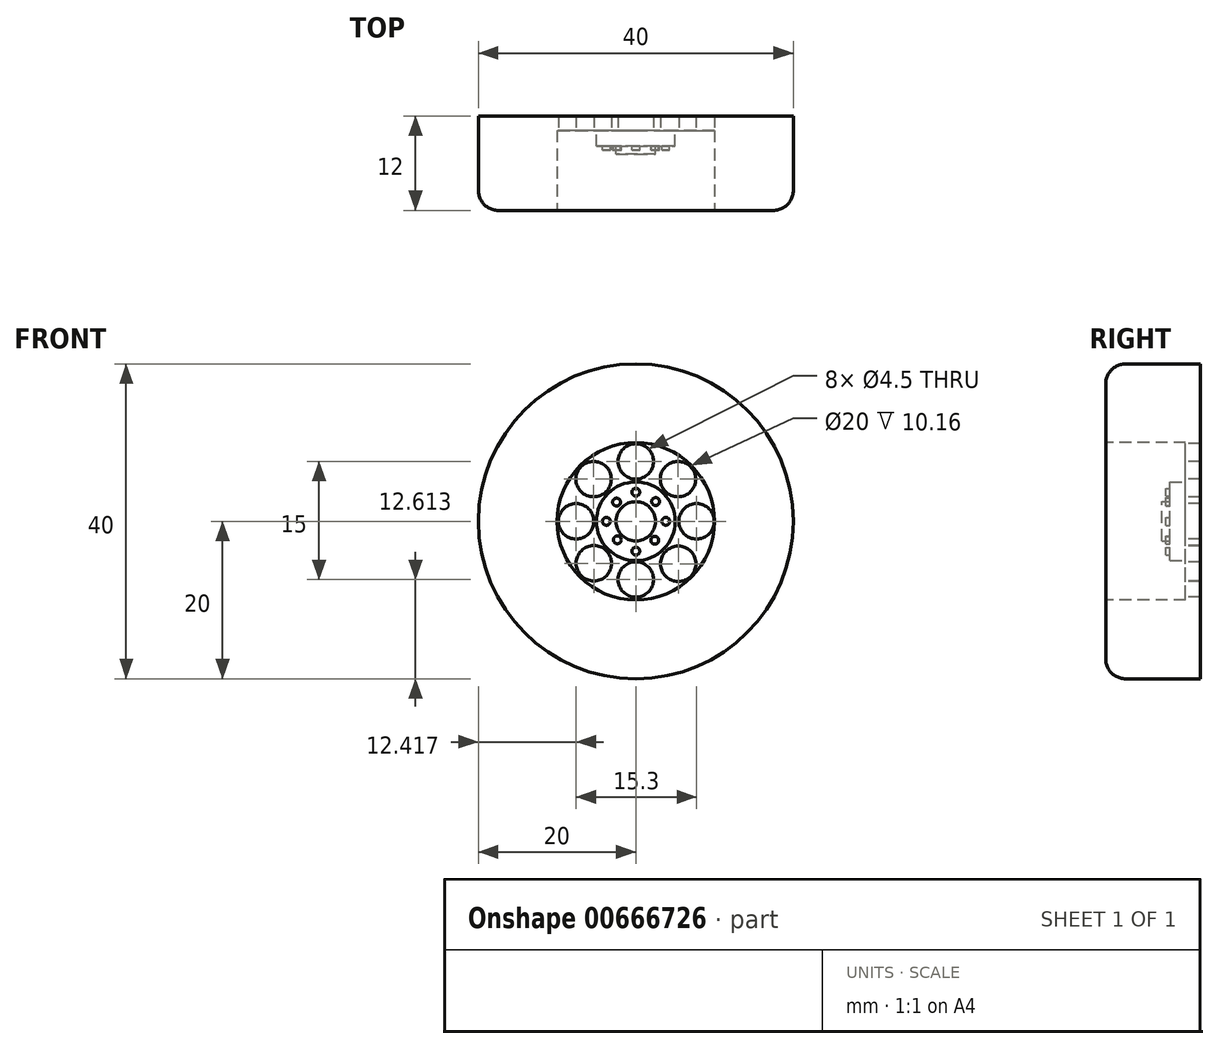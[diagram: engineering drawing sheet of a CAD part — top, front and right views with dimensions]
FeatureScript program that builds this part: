
annotation { "Feature Type Name" : "Feature", "Feature Type Description" : "" }
export const myFeature = defineFeature(function(context is Context, id is Id, definition is map)
    precondition{}
    {
        {
            var Q0;
            Q0=qCreatedBy(makeId("Front.planeOp"),FACE);
            var sketch = newSketch(context, id + "F0", { "sketchPlane" : qUnion([Q0])});
            skCircle(sketch, "E0", {"center": v(0, 0) * mm, "radius": 20 * mm});
            skSolve(sketch);
        }
        {
            var Q0;
            Q0=makeQuery(id+"F0.imprint","IMPRINT",FACE,{"disambiguationData":[TD([[makeQuery(id+"F0.imprint","IMPRINT",EDGE,{"derivedFrom":sQuery(id+"F0.wireOp",EDGE,"E0")}),1.0]])]});
            extrude(context, id + "F1", {"entities" : qUnion([Q0]), "depth" : 12 * mm, "offsetDistance" : 25.4 * mm});
        }
        {
            var Q0;
            Q0=makeQuery(id+"F1.opExtrude","CAP_FACE",FACE,{"disambiguationData":[OSD([sQuery(id+"F0.wireOp",EDGE,"E0")])],"isStart":false});
            fillet(context, id + "F2", {"entities" : qUnion([Q0]), "radius" : 2.54 * mm, "tangentPropagation" : true, "allowEdgeOverflow" : false});
        }
        {
            var Q0;
            Q0=makeQuery(id+"F1.opExtrude","CAP_FACE",FACE,{"disambiguationData":[OSD([sQuery(id+"F0.wireOp",EDGE,"E0")])],"isStart":false});
            var sketch = newSketch(context, id + "F3", { "sketchPlane" : qUnion([Q0])});
            skCircle(sketch, "E1", {"center": v(0, 0) * mm, "radius": 10 * mm});
            skSolve(sketch);
        }
        {
            var Q0;
            Q0=makeQuery(id+"F3.imprint","IMPRINT",FACE,{"disambiguationData":[TD([[makeQuery(id+"F3.imprint","IMPRINT",EDGE,{"derivedFrom":sQuery(id+"F3.wireOp",EDGE,"E1")}),1.0]])]});
            extrude(context, id + "F4", {"entities" : qUnion([Q0]), "operationType" : NewBodyOperationType.REMOVE, "oppositeDirection" : true, "depth" : 10.16 * mm, "offsetDistance" : 25.4 * mm});
        }
        {
            var Q0;
            Q0=makeQuery(id+"F4.boolean.opBoolean","COPY",FACE,{"derivedFrom":makeQuery(id+"F4.opExtrude","CAP_FACE",FACE,{"disambiguationData":[OSD([sQuery(id+"F3.wireOp",EDGE,"E1")])],"isStart":false})});
            var sketch = newSketch(context, id + "F5", { "sketchPlane" : qUnion([Q0])});
            skCircle(sketch, "E2.0.0", {"center": v(0, 0) * mm, "radius": 10 * mm});
            skCircle(sketch, "E3", {"center": v(0, 0) * mm, "radius": 5 * mm});
            skSolve(sketch);
        }
        {
            var Q0;
            Q0=makeQuery(id+"F5.imprint","IMPRINT",FACE,{"disambiguationData":[TD([[makeQuery(id+"F5.imprint","IMPRINT",EDGE,{"derivedFrom":sQuery(id+"F5.wireOp",EDGE,"E3")}),1.0]])]});
            extrude(context, id + "F6", {"entities" : qUnion([Q0]), "operationType" : NewBodyOperationType.ADD, "depth" : 2 * mm, "offsetDistance" : 25.4 * mm});
        }
        {
            var Q0;
            Q0=makeQuery(id+"F6.opExtrude","CAP_FACE",FACE,{"disambiguationData":[OSD([sQuery(id+"F5.wireOp",EDGE,"E3")])],"isStart":false});
            var sketch = newSketch(context, id + "F7", { "sketchPlane" : qUnion([Q0])});
            skCircle(sketch, "E4.0.0", {"center": v(0, 0) * mm, "radius": 5 * mm});
            skCircle(sketch, "E5", {"center": v(0, 0) * mm, "radius": 2.5 * mm});
            skSolve(sketch);
        }
        {
            var Q0;
            Q0=makeQuery(id+"F7.imprint","IMPRINT",FACE,{"disambiguationData":[TD([[makeQuery(id+"F7.imprint","IMPRINT",EDGE,{"derivedFrom":sQuery(id+"F7.wireOp",EDGE,"E5")}),1.0]])]});
            extrude(context, id + "F8", {"entities" : qUnion([Q0]), "operationType" : NewBodyOperationType.ADD, "depth" : 1 * mm, "offsetDistance" : 25.4 * mm});
        }
        {
            var Q0;
            Q0=makeQuery(id+"F4.boolean.opBoolean","COPY",FACE,{"derivedFrom":makeQuery(id+"F4.opExtrude","CAP_FACE",FACE,{"disambiguationData":[OSD([sQuery(id+"F3.wireOp",EDGE,"E1")])],"isStart":false})});
            var sketch = newSketch(context, id + "F9", { "sketchPlane" : qUnion([Q0])});
            skLineSegment(sketch, "E6", {"start": v(-7.58, 0) * mm, "end": v(7.72, 0) * mm});
            skLineSegment(sketch, "E7", {"start": v(0, 7.61) * mm, "end": v(0, -7.39) * mm});
            skSolve(sketch);
        }
        {
            var Q0;
            Q0=makeQuery(id+"F9.imprint","IMPRINT",FACE,{"disambiguationData":[TD([[makeQuery(id+"F9.imprint","IMPRINT",EDGE,{"derivedFrom":makeQuery(id+"F4.boolean.opBoolean","COPY",EDGE,{"derivedFrom":makeQuery(id+"F4.opExtrude","CAP_EDGE",EDGE,{"disambiguationData":[OSD([sQuery(id+"F3.wireOp",EDGE,"E1")])],"isStart":false})})}),1.0]])]});
            var sketch = newSketch(context, id + "F10", { "sketchPlane" : qUnion([Q0])});
            skPoint(sketch, "E8.0", {"position": v(0, 7.61) * mm});
            skPoint(sketch, "E9.0", {"position": v(-7.58, 0) * mm});
            skPoint(sketch, "E10.0", {"position": v(0, -7.39) * mm});
            skPoint(sketch, "E11.0", {"position": v(7.72, 0) * mm});
            skCircle(sketch, "E12", {"center": v(0, 7.61) * mm, "radius": 2.25 * mm});
            skCircle(sketch, "E13", {"center": v(7.72, 0) * mm, "radius": 2.25 * mm});
            skCircle(sketch, "E14", {"center": v(0, -7.39) * mm, "radius": 2.25 * mm});
            skCircle(sketch, "E15", {"center": v(-7.58, 0) * mm, "radius": 2.25 * mm});
            skSolve(sketch);
        }
        {
            var Q0;
            Q0=makeQuery(id+"F9.imprint","IMPRINT",FACE,{"disambiguationData":[TD([[makeQuery(id+"F9.imprint","IMPRINT",EDGE,{"derivedFrom":makeQuery(id+"F4.boolean.opBoolean","COPY",EDGE,{"derivedFrom":makeQuery(id+"F4.opExtrude","CAP_EDGE",EDGE,{"disambiguationData":[OSD([sQuery(id+"F3.wireOp",EDGE,"E1")])],"isStart":false})})}),1.0]])]});
            var sketch = newSketch(context, id + "F11", { "sketchPlane" : qUnion([Q0])});
            skCircle(sketch, "E16.0.0", {"center": v(0, 0) * mm, "radius": 10 * mm});
            skLineSegment(sketch, "E17", {"start": v(0, 0) * mm, "end": v(5.36, 5.36) * mm});
            skLineSegment(sketch, "E18", {"start": v(5.36, 5.36) * mm, "end": v(-5.33, -5.33) * mm});
            skLineSegment(sketch, "E19", {"start": v(0, 0) * mm, "end": v(-5.36, 5.36) * mm});
            skLineSegment(sketch, "E20", {"start": v(-5.36, 5.36) * mm, "end": v(5.4, -5.4) * mm});
            skCircle(sketch, "E21", {"center": v(-5.36, 5.36) * mm, "radius": 2.25 * mm});
            skCircle(sketch, "E22", {"center": v(5.36, 5.36) * mm, "radius": 2.25 * mm});
            skCircle(sketch, "E23", {"center": v(5.4, -5.4) * mm, "radius": 2.25 * mm});
            skCircle(sketch, "E24", {"center": v(-5.33, -5.33) * mm, "radius": 2.25 * mm});
            skSolve(sketch);
        }
        {
            var Q0;
            Q0 = qSketchRegion(id + "F10", true);
            extrude(context, id + "F12", {"entities" : qUnion([Q0]), "operationType" : NewBodyOperationType.REMOVE, "oppositeDirection" : true, "depth" : 25.4 * mm, "offsetDistance" : 25.4 * mm});
        }
        {
            var Q0;
            Q0=makeQuery(id+"F11.imprint","IMPRINT",FACE,{"disambiguationData":[TD([[makeQuery(id+"F11.imprint","IMPRINT",EDGE,{"derivedFrom":sQuery(id+"F11.wireOp",EDGE,"E22")}),1.0]])]});
            var Q1;
            Q1=makeQuery(id+"F11.imprint","IMPRINT",FACE,{"disambiguationData":[TD([[makeQuery(id+"F11.imprint","IMPRINT",EDGE,{"derivedFrom":sQuery(id+"F11.wireOp",EDGE,"E21")}),1.0]])]});
            var Q2;
            Q2=makeQuery(id+"F11.imprint","IMPRINT",FACE,{"disambiguationData":[TD([[makeQuery(id+"F11.imprint","IMPRINT",EDGE,{"derivedFrom":sQuery(id+"F11.wireOp",EDGE,"E24")}),1.0]])]});
            var Q3;
            Q3=makeQuery(id+"F11.imprint","IMPRINT",FACE,{"disambiguationData":[TD([[makeQuery(id+"F11.imprint","IMPRINT",EDGE,{"derivedFrom":sQuery(id+"F11.wireOp",EDGE,"E23")}),1.0]])]});
            extrude(context, id + "F13", {"entities" : qUnion([Q0, Q1, Q2, Q3]), "operationType" : NewBodyOperationType.REMOVE, "oppositeDirection" : true, "depth" : 25.4 * mm, "offsetDistance" : 25.4 * mm});
        }
        {
            var Q0;
            Q0=makeQuery(id+"F6.opExtrude","CAP_FACE",FACE,{"disambiguationData":[OSD([sQuery(id+"F5.wireOp",EDGE,"E3")])],"isStart":false});
            var sketch = newSketch(context, id + "F14", { "sketchPlane" : qUnion([Q0])});
            skLineSegment(sketch, "E25", {"start": v(0, 0) * mm, "end": v(0, 3.7) * mm});
            skLineSegment(sketch, "E26", {"start": v(0, 3.7) * mm, "end": v(0, -3.8) * mm});
            skLineSegment(sketch, "E27", {"start": v(0, 0) * mm, "end": v(-3.74, 0) * mm});
            skLineSegment(sketch, "E28", {"start": v(-3.74, 0) * mm, "end": v(0, 0) * mm});
            skLineSegment(sketch, "E29", {"start": v(0, 0) * mm, "end": v(0, 0) * mm});
            skLineSegment(sketch, "E30", {"start": v(0, 0) * mm, "end": v(-2.44, 2.44) * mm});
            skLineSegment(sketch, "E31", {"start": v(-2.44, 2.44) * mm, "end": v(2.4, -2.4) * mm});
            skLineSegment(sketch, "E32", {"start": v(0, 0) * mm, "end": v(2.52, 2.52) * mm});
            skLineSegment(sketch, "E33", {"start": v(2.52, 2.52) * mm, "end": v(-2.35, -2.35) * mm});
            skCircle(sketch, "E34", {"center": v(0, 3.7) * mm, "radius": 0.5 * mm});
            skCircle(sketch, "E35", {"center": v(2.52, 2.52) * mm, "radius": 0.5 * mm});
            skCircle(sketch, "E36", {"center": v(2.4, -2.4) * mm, "radius": 0.5 * mm});
            skCircle(sketch, "E37", {"center": v(0, -3.8) * mm, "radius": 0.5 * mm});
            skCircle(sketch, "E38", {"center": v(-2.35, -2.35) * mm, "radius": 0.5 * mm});
            skCircle(sketch, "E39", {"center": v(-3.74, 0) * mm, "radius": 0.5 * mm});
            skCircle(sketch, "E40", {"center": v(-2.44, 2.44) * mm, "radius": 0.5 * mm});
            skLineSegment(sketch, "E41", {"start": v(0, 0) * mm, "end": v(3.8, 0) * mm});
            skCircle(sketch, "E42", {"center": v(3.8, 0) * mm, "radius": 0.5 * mm});
            skSolve(sketch);
        }
        {
            var Q0;
            Q0=makeQuery(id+"F14.imprint","IMPRINT",FACE,{"disambiguationData":[TD([[makeQuery(id+"F14.imprint","IMPRINT",EDGE,{"derivedFrom":sQuery(id+"F14.wireOp",EDGE,"E34")}),1.0]])]});
            var Q1;
            Q1=makeQuery(id+"F14.imprint","IMPRINT",FACE,{"disambiguationData":[TD([[makeQuery(id+"F14.imprint","IMPRINT",EDGE,{"derivedFrom":sQuery(id+"F14.wireOp",EDGE,"E35")}),1.0]])]});
            var Q2;
            Q2=makeQuery(id+"F14.imprint","IMPRINT",FACE,{"disambiguationData":[TD([[makeQuery(id+"F14.imprint","IMPRINT",EDGE,{"derivedFrom":sQuery(id+"F14.wireOp",EDGE,"E42")}),1.0]])]});
            var Q3;
            Q3=makeQuery(id+"F14.imprint","IMPRINT",FACE,{"disambiguationData":[TD([[makeQuery(id+"F14.imprint","IMPRINT",EDGE,{"derivedFrom":sQuery(id+"F14.wireOp",EDGE,"E36")}),1.0]])]});
            var Q4;
            Q4=makeQuery(id+"F14.imprint","IMPRINT",FACE,{"disambiguationData":[TD([[makeQuery(id+"F14.imprint","IMPRINT",EDGE,{"derivedFrom":sQuery(id+"F14.wireOp",EDGE,"E37")}),1.0]])]});
            var Q5;
            Q5=makeQuery(id+"F14.imprint","IMPRINT",FACE,{"disambiguationData":[TD([[makeQuery(id+"F14.imprint","IMPRINT",EDGE,{"derivedFrom":sQuery(id+"F14.wireOp",EDGE,"E38")}),1.0]])]});
            var Q6;
            Q6=makeQuery(id+"F14.imprint","IMPRINT",FACE,{"disambiguationData":[TD([[makeQuery(id+"F14.imprint","IMPRINT",EDGE,{"derivedFrom":sQuery(id+"F14.wireOp",EDGE,"E39")}),1.0]])]});
            var Q7;
            Q7=makeQuery(id+"F14.imprint","IMPRINT",FACE,{"disambiguationData":[TD([[makeQuery(id+"F14.imprint","IMPRINT",EDGE,{"derivedFrom":sQuery(id+"F14.wireOp",EDGE,"E40")}),1.0]])]});
            extrude(context, id + "F15", {"entities" : qUnion([Q0, Q1, Q2, Q3, Q4, Q5, Q6, Q7]), "operationType" : NewBodyOperationType.ADD, "depth" : .5 * mm, "offsetDistance" : 25.4 * mm});
        }
    });
